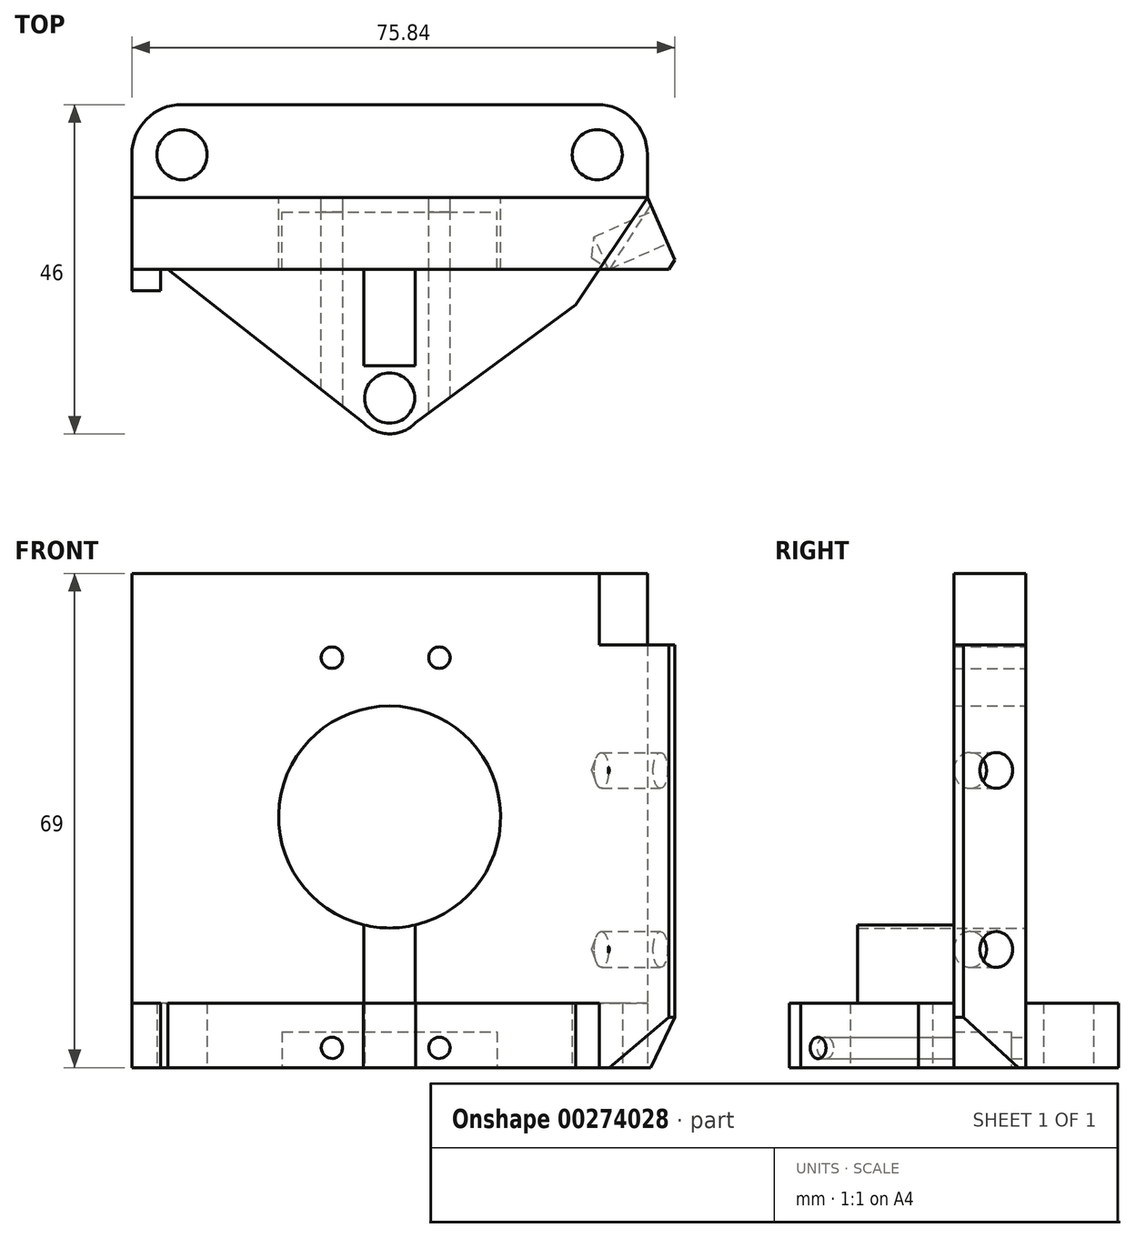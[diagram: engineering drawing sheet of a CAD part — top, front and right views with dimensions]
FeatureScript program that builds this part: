
annotation { "Feature Type Name" : "Feature", "Feature Type Description" : "" }
export const myFeature = defineFeature(function(context is Context, id is Id, definition is map)
    precondition{}
    {
        {
            var Q0;
            Q0=qCreatedBy(makeId("Top.planeOp"),FACE);
            var sketch = newSketch(context, id + "F0", { "sketchPlane" : qUnion([Q0])});
            skLineSegment(sketch, "E0", {"start": v(-36, -26) * mm, "end": v(-32, -26) * mm});
            skLineSegment(sketch, "E1", {"start": v(-32, -26) * mm, "end": v(-32, -23) * mm});
            skLineSegment(sketch, "E2", {"start": v(-32, -23) * mm, "end": v(-31, -23) * mm});
            skLineSegment(sketch, "E3", {"start": v(-31, -23) * mm, "end": v(-3.64, -44.43) * mm});
            skLineSegment(sketch, "E4", {"start": v(-29, 0) * mm, "end": v(29, 0) * mm});
            skLineSegment(sketch, "E5", {"start": v(-36, -26) * mm, "end": v(-36, -7) * mm});
            skCircle(sketch, "E6", {"center": v(-29, -7) * mm, "radius": 3.5 * mm});
            skCircle(sketch, "E7", {"center": v(29, -7) * mm, "radius": 3.5 * mm});
            skCircle(sketch, "E8", {"center": v(0, -41) * mm, "radius": 3.5 * mm});
            skArc(sketch, "E9", {"start": v(-3.64, -44.43) * mm, "mid": v(0, -46) * mm, "end": v(3.64, -44.43) * mm});
            skArc(sketch, "E10", {"start": v(-36, -7) * mm, "mid": v(-33.95, -2.05) * mm, "end": v(-29, 0) * mm});
            skArc(sketch, "E11", {"start": v(29, 0) * mm, "mid": v(33.95, -2.05) * mm, "end": v(36, -7) * mm});
            skLineSegment(sketch, "E12", {"start": v(26, -27.97) * mm, "end": v(3.64, -44.43) * mm});
            skLineSegment(sketch, "E13", {"start": v(26, -27.97) * mm, "end": v(36, -13) * mm});
            skLineSegment(sketch, "E14", {"start": v(36, -13) * mm, "end": v(36, -7) * mm});
            skSolve(sketch);
        }
        {
            var Q0;
            Q0 = qSketchRegion(id + "F0", true);
            extrude(context, id + "F1", {"entities" : qUnion([Q0]), "depth" : 9 * mm});
        }
        {
            var Q0;
            Q0=makeQuery(id+"F0.imprint","IMPRINT",FACE,{"disambiguationData":[TD([[makeQuery(id+"F0.imprint","IMPRINT",EDGE,{"derivedFrom":sQuery(id+"F0.wireOp",EDGE,"E0")}),1.0]])]});
            var sketch = newSketch(context, id + "F2", { "sketchPlane" : qUnion([Q0])});
            skLineSegment(sketch, "E15.bottom", {"start": v(-15, -23) * mm, "end": v(15, -23) * mm});
            skLineSegment(sketch, "E15.top", {"start": v(-15, -15) * mm, "end": v(15, -15) * mm});
            skLineSegment(sketch, "E15.left", {"start": v(-15, -23) * mm, "end": v(-15, -15) * mm});
            skLineSegment(sketch, "E15.right", {"start": v(15, -23) * mm, "end": v(15, -15) * mm});
            skPoint(sketch, "E15.middle", {"position": v(0, -19) * mm});
            skSolve(sketch);
        }
        {
            var Q0;
            Q0 = qSketchRegion(id + "F2", true);
            extrude(context, id + "F3", {"entities" : qUnion([Q0]), "operationType" : NewBodyOperationType.REMOVE, "depth" : 5 * mm});
        }
        {
            var Q0;
            Q0=makeQuery(id+"F1.opExtrude","CAP_FACE",FACE,{"disambiguationData":[OSD([sQuery(id+"F0.wireOp",EDGE,"E0"),sQuery(id+"F0.wireOp",EDGE,"E1"),sQuery(id+"F0.wireOp",EDGE,"E2"),sQuery(id+"F0.wireOp",EDGE,"E3"),sQuery(id+"F0.wireOp",EDGE,"E4"),sQuery(id+"F0.wireOp",EDGE,"E5"),sQuery(id+"F0.wireOp",EDGE,"E6"),sQuery(id+"F0.wireOp",EDGE,"E7"),sQuery(id+"F0.wireOp",EDGE,"E8"),sQuery(id+"F0.wireOp",EDGE,"E9"),sQuery(id+"F0.wireOp",EDGE,"E10"),sQuery(id+"F0.wireOp",EDGE,"E11"),sQuery(id+"F0.wireOp",EDGE,"WJA2m645-39Qq-lADn-E0cL-840yLO94TB4h"),sQuery(id+"F0.wireOp",EDGE,"E12")])],"isStart":false});
            var sketch = newSketch(context, id + "F4", { "sketchPlane" : qUnion([Q0])});
            skPoint(sketch, "E16.middle.positionSnap0", {"position": v(0, 0) * mm});
            skPoint(sketch, "E16.centerSnap0", {"position": v(0, 0) * mm});
            skLineSegment(sketch, "E17", {"start": v(-36, -13) * mm, "end": v(36, -13) * mm});
            skLineSegment(sketch, "E18", {"start": v(36, -13) * mm, "end": v(39.84, -21.7) * mm});
            skLineSegment(sketch, "E19", {"start": v(39.84, -21.7) * mm, "end": v(39, -23) * mm});
            skLineSegment(sketch, "E20", {"start": v(39, -23) * mm, "end": v(-36, -23) * mm});
            skLineSegment(sketch, "E21", {"start": v(-36, -13) * mm, "end": v(-36, -23) * mm});
            skSolve(sketch);
        }
        {
            var Q0;
            {var subQ7=sQuery(id+"F4.wireOp",EDGE,"E17");Q0=makeQuery(id+"F4.imprint","IMPRINT",FACE,{"disambiguationData":[TD([[makeQuery(id+"F4.imprint","IMPRINT",EDGE,{"derivedFrom":subQ7}),-1.0]])]});}
            var Q1;
            {var subQ0=sQuery(id+"F4.wireOp",EDGE,"E21");Q1=makeQuery(id+"F4.imprint","IMPRINT",FACE,{"disambiguationData":[TD([[makeQuery(id+"F4.imprint","IMPRINT",EDGE,{"derivedFrom":subQ0}),-1.0]])]});}
            extrude(context, id + "F5", {"entities" : qUnion([Q0, Q1]), "operationType" : NewBodyOperationType.ADD, "depth" : 60 * mm});
        }
        {
            var Q0;
            {var subQ3=sQuery(id+"F4.wireOp",EDGE,"E18");Q0=makeQuery(id+"F4.imprint","IMPRINT",FACE,{"disambiguationData":[TD([[makeQuery(id+"F4.imprint","IMPRINT",EDGE,{"derivedFrom":subQ3}),-1.0]])]});}
            extrude(context, id + "F6", {"entities" : qUnion([Q0]), "operationType" : NewBodyOperationType.ADD, "depth" : 50 * mm});
        }
        {
            var Q0;
            {var subQ3=sQuery(id+"F4.wireOp",EDGE,"E18");Q0=makeQuery(id+"F4.imprint","IMPRINT",FACE,{"disambiguationData":[TD([[makeQuery(id+"F4.imprint","IMPRINT",EDGE,{"derivedFrom":subQ3}),-1.0]])]});}
            extrude(context, id + "F7", {"entities" : qUnion([Q0]), "operationType" : NewBodyOperationType.ADD, "oppositeDirection" : true, "depth" : 9 * mm});
        }
        {
            var Q0;
            Q0=makeQuery(id+"F7.opExtrude","CAP_EDGE",EDGE,{"disambiguationData":[OSD([sQuery(id+"F4.wireOp",EDGE,"E19")])],"isStart":false});
            chamfer(context, id + "F8", {"entities" : qUnion([Q0]), "width" : 7 * mm, "tangentPropagation" : true});
        }
        {
            var Q0;
            {var subQ0=sQuery(id+"F4.wireOp",EDGE,"E18");Q0=makeQuery(id+"F7.boolean.opBoolean","MERGE",FACE,{"derivedFrom":[makeQuery(id+"F6.opExtrude","SWEPT_FACE",FACE,{"disambiguationData":[OSD([subQ0])]}),makeQuery(id+"F7.opExtrude","SWEPT_FACE",FACE,{"disambiguationData":[OSD([subQ0])]})]});}
            var sketch = newSketch(context, id + "F9", { "sketchPlane" : qUnion([Q0])});
            skPoint(sketch, "E22", {"position": v(-30.93, 41.5) * mm});
            skPoint(sketch, "E23", {"position": v(-30.93, 16.5) * mm});
            skSolve(sketch);
        }
        {
            var Q0;
            Q0=sQuery(id+"F9.wireOp",VERTEX,"E23");
            var Q1;
            Q1=sQuery(id+"F9.wireOp",VERTEX,"E22");
            var Q2;
            Q2=makeQuery(id+"F1.opExtrude","SWEPT_BODY",BODY,{"disambiguationData":[OSD([sQuery(id+"F0.wireOp",EDGE,"E0"),sQuery(id+"F0.wireOp",EDGE,"E1"),sQuery(id+"F0.wireOp",EDGE,"E2"),sQuery(id+"F0.wireOp",EDGE,"E3"),sQuery(id+"F0.wireOp",EDGE,"E4"),sQuery(id+"F0.wireOp",EDGE,"E5"),sQuery(id+"F0.wireOp",EDGE,"E6"),sQuery(id+"F0.wireOp",EDGE,"E7"),sQuery(id+"F0.wireOp",EDGE,"E8"),sQuery(id+"F0.wireOp",EDGE,"E9"),sQuery(id+"F0.wireOp",EDGE,"E10"),sQuery(id+"F0.wireOp",EDGE,"E11"),sQuery(id+"F0.wireOp",EDGE,"E12"),sQuery(id+"F0.wireOp",EDGE,"E13"),sQuery(id+"F0.wireOp",EDGE,"E14")])]});
            hole(context, id + "F10", {"style" : HoleStyle.SIMPLE, "endStyle" : HoleEndStyle.BLIND, "holeDiameter" : 5 * mm, "holeDepth" : 9 * mm, "tappedDepth" : 12 * mm, "tapClearance" : 3, "startFromSketch" : true, "locations" : qUnion([Q0, Q1]), "scope" : qUnion([Q2])});
        }
        {
            var Q0;
            {var subQ0=sQuery(id+"F0.wireOp",EDGE,"E9");var subQ1=sQuery(id+"F0.wireOp",EDGE,"E8");var subQ2=sQuery(id+"F0.wireOp",EDGE,"E3");var subQ3=sQuery(id+"F0.wireOp",EDGE,"E2");var subQ4=sQuery(id+"F0.wireOp",EDGE,"E13");var subQ5=sQuery(id+"F0.wireOp",EDGE,"E12");Q0=makeQuery(id+"F5.boolean.opBoolean","SPLIT",FACE,{"disambiguationData":[TD([makeQuery(id+"F1.opExtrude","SWEPT_FACE",FACE,{"disambiguationData":[OSD([subQ2])]})])],"derivedFrom":makeQuery(id+"F1.opExtrude","CAP_FACE",FACE,{"disambiguationData":[OSD([sQuery(id+"F0.wireOp",EDGE,"E0"),sQuery(id+"F0.wireOp",EDGE,"E1"),subQ3,subQ2,sQuery(id+"F0.wireOp",EDGE,"E4"),sQuery(id+"F0.wireOp",EDGE,"E5"),sQuery(id+"F0.wireOp",EDGE,"E6"),sQuery(id+"F0.wireOp",EDGE,"E7"),subQ1,subQ0,sQuery(id+"F0.wireOp",EDGE,"E10"),sQuery(id+"F0.wireOp",EDGE,"E11"),subQ5,subQ4,sQuery(id+"F0.wireOp",EDGE,"E14")])],"isStart":false})});}
            var sketch = newSketch(context, id + "F11", { "sketchPlane" : qUnion([Q0])});
            skLineSegment(sketch, "E24.bottom", {"start": v(3.6, -36.46) * mm, "end": v(-3.6, -36.46) * mm});
            skLineSegment(sketch, "E24.top", {"start": v(3.6, -19.46) * mm, "end": v(-3.6, -19.46) * mm});
            skLineSegment(sketch, "E24.left", {"start": v(3.6, -36.46) * mm, "end": v(3.6, -19.46) * mm});
            skLineSegment(sketch, "E24.right", {"start": v(-3.6, -36.46) * mm, "end": v(-3.6, -19.46) * mm});
            skPoint(sketch, "E24.middle", {"position": v(0, -27.96) * mm});
            skSolve(sketch);
        }
        {
            var Q0;
            Q0 = qSketchRegion(id + "F11", true);
            extrude(context, id + "F12", {"entities" : qUnion([Q0]), "operationType" : NewBodyOperationType.ADD, "depth" : 25 * mm});
        }
        {
            var Q0;
            Q0=makeQuery(id+"F5.opExtrude","SWEPT_FACE",FACE,{"disambiguationData":[OSD([sQuery(id+"F4.wireOp",EDGE,"E17")])]});
            var sketch = newSketch(context, id + "F13", { "sketchPlane" : qUnion([Q0])});
            skCircle(sketch, "E25", {"center": v(-6.95, 2.75) * mm, "radius": 1.5 * mm});
            skCircle(sketch, "E26", {"center": v(-6.95, 57.25) * mm, "radius": 1.5 * mm});
            skCircle(sketch, "E27", {"center": v(8.05, 57.25) * mm, "radius": 1.5 * mm});
            skCircle(sketch, "E28", {"center": v(8.05, 2.75) * mm, "radius": 1.5 * mm});
            skLineSegment(sketch, "E29.bottom", {"start": v(-9.7, 0) * mm, "end": v(-9.7, 60) * mm});
            skLineSegment(sketch, "E29.top", {"start": v(10.8, 0) * mm, "end": v(10.8, 60) * mm});
            skLineSegment(sketch, "E29.left", {"start": v(-9.7, 0) * mm, "end": v(10.8, 0) * mm});
            skLineSegment(sketch, "E29.right", {"start": v(-9.7, 60) * mm, "end": v(10.8, 60) * mm});
            skSolve(sketch);
        }
        {
            var Q0;
            Q0=makeQuery(id+"F13.imprint","IMPRINT",FACE,{"disambiguationData":[TD([[makeQuery(id+"F13.imprint","IMPRINT",EDGE,{"derivedFrom":sQuery(id+"F13.wireOp",EDGE,"E25")}),1.0]])]});
            var Q1;
            Q1=makeQuery(id+"F13.imprint","IMPRINT",FACE,{"disambiguationData":[TD([[makeQuery(id+"F13.imprint","IMPRINT",EDGE,{"derivedFrom":sQuery(id+"F13.wireOp",EDGE,"E28")}),1.0]])]});
            var Q2;
            Q2=makeQuery(id+"F13.imprint","IMPRINT",FACE,{"disambiguationData":[TD([[makeQuery(id+"F13.imprint","IMPRINT",EDGE,{"derivedFrom":sQuery(id+"F13.wireOp",EDGE,"E27")}),1.0]])]});
            var Q3;
            Q3=makeQuery(id+"F13.imprint","IMPRINT",FACE,{"disambiguationData":[TD([[makeQuery(id+"F13.imprint","IMPRINT",EDGE,{"derivedFrom":sQuery(id+"F13.wireOp",EDGE,"E26")}),1.0]])]});
            extrude(context, id + "F14", {"entities" : qUnion([Q0, Q1, Q2, Q3]), "operationType" : NewBodyOperationType.REMOVE, "endBound" : BoundingType.THROUGH_ALL, "oppositeDirection" : true, "depth" : 25 * mm});
        }
        {
            var Q0;
            {var subQ0=sQuery(id+"F0.wireOp",EDGE,"E10");var subQ1=sQuery(id+"F0.wireOp",EDGE,"E14");var subQ2=sQuery(id+"F0.wireOp",EDGE,"E13");var subQ3=sQuery(id+"F0.wireOp",EDGE,"E11");var subQ4=sQuery(id+"F0.wireOp",EDGE,"E4");var subQ5=sQuery(id+"F0.wireOp",EDGE,"E5");var subQ6=sQuery(id+"F0.wireOp",EDGE,"E6");var subQ7=sQuery(id+"F0.wireOp",EDGE,"E7");Q0=makeQuery(id+"F5.boolean.opBoolean","SPLIT",FACE,{"disambiguationData":[TD([makeQuery(id+"F1.opExtrude","SWEPT_FACE",FACE,{"disambiguationData":[OSD([subQ4])]})])],"derivedFrom":makeQuery(id+"F1.opExtrude","CAP_FACE",FACE,{"disambiguationData":[OSD([sQuery(id+"F0.wireOp",EDGE,"E0"),sQuery(id+"F0.wireOp",EDGE,"E1"),sQuery(id+"F0.wireOp",EDGE,"E2"),sQuery(id+"F0.wireOp",EDGE,"E3"),subQ4,subQ5,subQ6,subQ7,sQuery(id+"F0.wireOp",EDGE,"E8"),sQuery(id+"F0.wireOp",EDGE,"E9"),subQ0,subQ3,sQuery(id+"F0.wireOp",EDGE,"E12"),subQ2,subQ1])],"isStart":false})});}
            var sketch = newSketch(context, id + "F15", { "sketchPlane" : qUnion([Q0])});
            skSolve(sketch);
        }
        {
            var Q0;
            Q0=makeQuery(id+"FEbFz6zTrpfMZsp_1.boolean.opBoolean","MERGE",FACE,{"derivedFrom":[makeQuery(id+"F5.opExtrude","SWEPT_FACE",FACE,{"disambiguationData":[OSD([sQuery(id+"F4.wireOp",EDGE,"E17")])]}),makeQuery(id+"FEbFz6zTrpfMZsp_1.opExtrude","SWEPT_FACE",FACE,{"disambiguationData":[OSD([sQuery(id+"F15.wireOp",EDGE,"UuulbaJ0-uh5O-iian-63B3-8MHiHCaYlGRc.top")])]})]});
            var sketch = newSketch(context, id + "F16", { "sketchPlane" : qUnion([Q0])});
            skCircle(sketch, "E30", {"center": v(0, 35) * mm, "radius": 15.5 * mm});
            skSolve(sketch);
        }
        {
            var Q0;
            Q0 = qSketchRegion(id + "F16", true);
            extrude(context, id + "F17", {"entities" : qUnion([Q0]), "operationType" : NewBodyOperationType.REMOVE, "oppositeDirection" : true, "depth" : 25 * mm});
        }
    });
